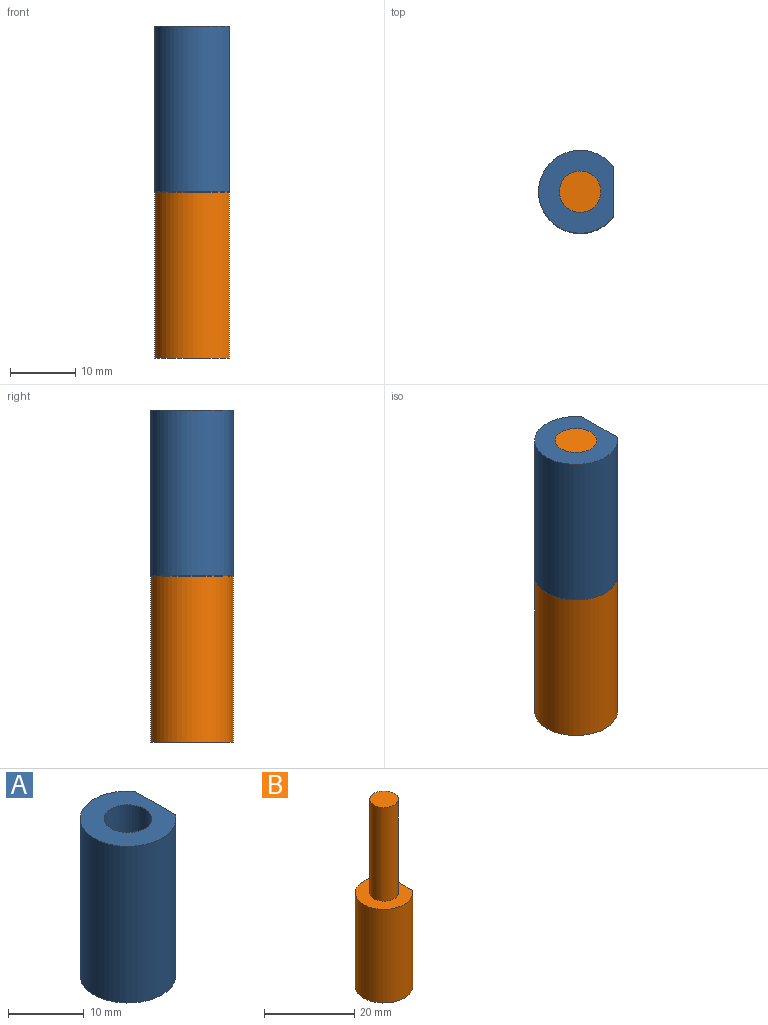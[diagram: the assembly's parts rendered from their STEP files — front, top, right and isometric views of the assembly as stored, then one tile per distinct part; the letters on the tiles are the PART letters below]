
ASSEMBLY  parts=2 mates=1
PART A: 5 faces, bbox 11.4x12.7x25.4 mm
  f0: cylinder r=6.35mm len=25.4mm, axis (0,0,-1), area 805.8mm2, adj f2,f3,f4
  f1: cylinder r=3.17mm len=25.4mm, axis (0,0,-1), area 506.7mm2, adj f3,f4
  f2: plane 25.4x7.62mm, normal (1,0,0), area 193.5mm2, adj f0,f3,f4
  f3: plane 12.7x11.43mm, normal (0,0,1), area 88.4mm2, adj f0,f1,f2
  f4: plane 12.7x11.43mm, normal (0,0,-1), area 88.4mm2, adj f0,f1,f2
PART B: 6 faces, bbox 11.4x12.7x50.8 mm
  f0: cylinder r=3.17mm len=25.4mm, axis (0,0,-1), area 506.7mm2, adj f1,f4
  f1: plane 6.35x6.35mm, normal (0,0,1), area 31.7mm2, adj f0
  f2: plane 25.4x7.62mm, normal (1,0,0), area 193.5mm2, adj f3,f4,f5
  f3: cylinder r=6.35mm len=25.4mm, axis (0,0,-1), area 805.8mm2, adj f2,f4,f5
  f4: plane 12.7x11.43mm, normal (0,0,1), area 88.4mm2, adj f0,f2,f3
  f5: plane 12.7x11.43mm, normal (0,0,-1), area 120.1mm2, adj f2,f3
PLACE A t=(14.43,-0.75,25.82)mm
PLACE B t=(14.43,-0.75,0.42)mm
MATE revolute A.f1 <-> B.f0  axis (0,0,-1) through (14.43,-0.75,51.22)mm
